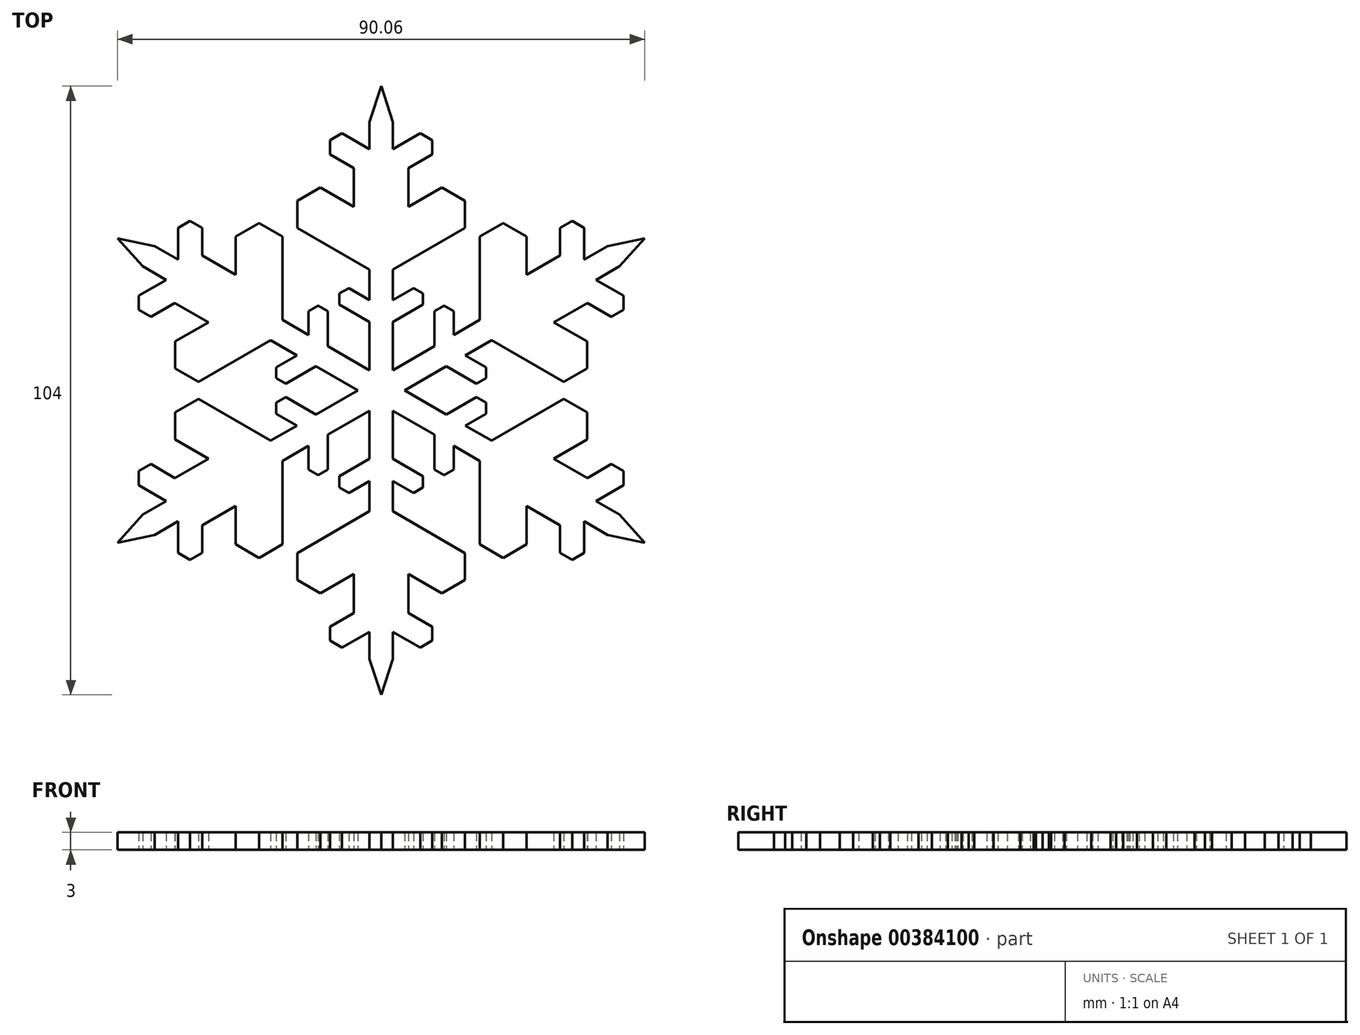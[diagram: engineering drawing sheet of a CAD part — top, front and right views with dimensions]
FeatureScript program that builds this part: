
annotation { "Feature Type Name" : "Feature", "Feature Type Description" : "" }
export const myFeature = defineFeature(function(context is Context, id is Id, definition is map)
    precondition{}
    {
        {
            var Q0;
            Q0=qCreatedBy(makeId("Top.planeOp"),FACE);
            var sketch = newSketch(context, id + "F0", { "sketchPlane" : qUnion([Q0])});
            skLineSegment(sketch, "E0", {"start": v(0, 26) * mm, "end": v(0, -26) * mm, "construction": true});
            skLineSegment(sketch, "E1", {"start": v(22.52, -13) * mm, "end": v(-22.52, 13) * mm, "construction": true});
            skLineSegment(sketch, "E2", {"start": v(-22.52, -13) * mm, "end": v(22.52, 13) * mm, "construction": true});
            skLineSegment(sketch, "E3", {"start": v(0, 26) * mm, "end": v(-1, 22.94) * mm});
            skLineSegment(sketch, "E4", {"start": v(-1, 22.94) * mm, "end": v(-1, 0.58) * mm});
            skLineSegment(sketch, "E5", {"start": v(-1, 10.33) * mm, "end": v(-7.17, 13.89) * mm});
            skLineSegment(sketch, "E6", {"start": v(-7.17, 13.89) * mm, "end": v(-7.17, 16.19) * mm});
            skLineSegment(sketch, "E7", {"start": v(-7.17, 16.19) * mm, "end": v(-5.18, 17.34) * mm});
            skLineSegment(sketch, "E8", {"start": v(-5.18, 17.34) * mm, "end": v(-2.34, 15.7) * mm});
            skLineSegment(sketch, "E9", {"start": v(-2.34, 15.7) * mm, "end": v(-2.34, 19) * mm});
            skLineSegment(sketch, "E10", {"start": v(-2.34, 19) * mm, "end": v(-4.38, 20.18) * mm});
            skLineSegment(sketch, "E11", {"start": v(-4.38, 20.18) * mm, "end": v(-4.38, 21.38) * mm});
            skLineSegment(sketch, "E12", {"start": v(-4.38, 21.38) * mm, "end": v(-3.34, 21.98) * mm});
            skLineSegment(sketch, "E13", {"start": v(-3.34, 21.98) * mm, "end": v(-1, 20.62) * mm});
            skLineSegment(sketch, "E14", {"start": v(-7.17, 13.89) * mm, "end": v(-5.18, 17.34) * mm, "construction": true});
            skLineSegment(sketch, "E15", {"start": v(-7.17, 16.19) * mm, "end": v(-6.18, 15.61) * mm, "construction": true});
            skLineSegment(sketch, "E16", {"start": v(-4.38, 20.18) * mm, "end": v(-3.34, 21.98) * mm, "construction": true});
            skLineSegment(sketch, "E17", {"start": v(-4.38, 21.38) * mm, "end": v(-3.86, 21.08) * mm, "construction": true});
            skLineSegment(sketch, "E18", {"start": v(-1, 7.73) * mm, "end": v(-2.76, 8.75) * mm});
            skLineSegment(sketch, "E19", {"start": v(-2.76, 8.75) * mm, "end": v(-3.58, 8.28) * mm});
            skLineSegment(sketch, "E20", {"start": v(-3.58, 8.28) * mm, "end": v(-3.58, 7.34) * mm});
            skLineSegment(sketch, "E21", {"start": v(-3.58, 7.34) * mm, "end": v(-1, 5.85) * mm});
            skLineSegment(sketch, "E22", {"start": v(-2.76, 8.75) * mm, "end": v(-3.58, 7.34) * mm, "construction": true});
            skLineSegment(sketch, "E23", {"start": v(-3.58, 8.28) * mm, "end": v(-3.17, 8.04) * mm, "construction": true});
            skLineSegment(sketch, "E24.MirrorCS", {"start": v(4.38, 20.18) * mm, "end": v(3.34, 21.98) * mm, "construction": true});
            skLineSegment(sketch, "E25.MirrorCS", {"start": v(3.58, 8.28) * mm, "end": v(3.58, 7.34) * mm});
            skLineSegment(sketch, "E26.MirrorCS", {"start": v(2.76, 8.75) * mm, "end": v(3.58, 7.34) * mm, "construction": true});
            skLineSegment(sketch, "E27.MirrorCS", {"start": v(3.58, 8.28) * mm, "end": v(3.17, 8.04) * mm, "construction": true});
            skLineSegment(sketch, "E28.MirrorCS", {"start": v(4.38, 21.38) * mm, "end": v(3.34, 21.98) * mm});
            skLineSegment(sketch, "E29.MirrorCS", {"start": v(2.76, 8.75) * mm, "end": v(3.58, 8.28) * mm});
            skLineSegment(sketch, "E30.MirrorCS", {"start": v(4.38, 20.18) * mm, "end": v(4.38, 21.38) * mm});
            skLineSegment(sketch, "E31.MirrorCS", {"start": v(4.38, 21.38) * mm, "end": v(3.86, 21.08) * mm, "construction": true});
            skLineSegment(sketch, "E32.MirrorCS", {"start": v(1, 7.73) * mm, "end": v(2.76, 8.75) * mm});
            skLineSegment(sketch, "E33.MirrorCS", {"start": v(7.17, 16.19) * mm, "end": v(6.18, 15.61) * mm, "construction": true});
            skLineSegment(sketch, "E34.MirrorCS", {"start": v(2.34, 19) * mm, "end": v(4.38, 20.18) * mm});
            skLineSegment(sketch, "E35.MirrorCS", {"start": v(3.58, 7.34) * mm, "end": v(1, 5.85) * mm});
            skLineSegment(sketch, "E36.MirrorCS", {"start": v(7.17, 13.89) * mm, "end": v(5.18, 17.34) * mm, "construction": true});
            skLineSegment(sketch, "E37.MirrorCS", {"start": v(0, 26) * mm, "end": v(1, 22.94) * mm});
            skLineSegment(sketch, "E38.MirrorCS", {"start": v(2.34, 15.7) * mm, "end": v(2.34, 19) * mm});
            skLineSegment(sketch, "E39.MirrorCS", {"start": v(1, 22.94) * mm, "end": v(1, 0.58) * mm});
            skLineSegment(sketch, "E40.MirrorCS", {"start": v(7.17, 13.89) * mm, "end": v(7.17, 16.19) * mm});
            skLineSegment(sketch, "E41.MirrorCS", {"start": v(5.18, 17.34) * mm, "end": v(2.34, 15.7) * mm});
            skLineSegment(sketch, "E42.MirrorCS", {"start": v(1, 10.33) * mm, "end": v(7.17, 13.89) * mm});
            skLineSegment(sketch, "E43.MirrorCS", {"start": v(7.17, 16.19) * mm, "end": v(5.18, 17.34) * mm});
            skLineSegment(sketch, "E44.MirrorCS", {"start": v(3.34, 21.98) * mm, "end": v(1, 20.62) * mm});
            skLineSegment(sketch, "E45.1.0", {"start": v(-17.6, 1.88) * mm, "end": v(-17.6, 4.18) * mm});
            skLineSegment(sketch, "E45.1.1", {"start": v(-4.56, 6.77) * mm, "end": v(-4.56, 3.79) * mm});
            skLineSegment(sketch, "E45.1.2", {"start": v(-9.44, 4.3) * mm, "end": v(-15.61, 0.73) * mm});
            skLineSegment(sketch, "E45.1.3", {"start": v(-15.61, 0.73) * mm, "end": v(-17.6, 1.88) * mm});
            skLineSegment(sketch, "E45.1.4", {"start": v(-8.44, 6.03) * mm, "end": v(-8.44, 13.15) * mm});
            skLineSegment(sketch, "E45.1.5", {"start": v(-17.6, 4.18) * mm, "end": v(-14.76, 5.82) * mm});
            skLineSegment(sketch, "E45.1.6", {"start": v(-20.36, 10.6) * mm, "end": v(-1, -0.58) * mm});
            skLineSegment(sketch, "E45.1.7", {"start": v(-22.52, 13) * mm, "end": v(-20.36, 10.6) * mm});
            skLineSegment(sketch, "E45.1.8", {"start": v(-14.76, 5.82) * mm, "end": v(-17.62, 7.47) * mm});
            skLineSegment(sketch, "E45.1.9", {"start": v(-8.44, 13.15) * mm, "end": v(-12.42, 13.15) * mm, "construction": true});
            skLineSegment(sketch, "E45.1.10", {"start": v(-15.61, 0.73) * mm, "end": v(-17.6, 4.18) * mm, "construction": true});
            skLineSegment(sketch, "E45.1.11", {"start": v(-20.7, 8.1) * mm, "end": v(-18.36, 9.45) * mm});
            skLineSegment(sketch, "E45.1.12", {"start": v(-19.36, 12.34) * mm, "end": v(0, 1.15) * mm});
            skLineSegment(sketch, "E45.1.13", {"start": v(-10.43, 14.3) * mm, "end": v(-12.42, 13.15) * mm});
            skLineSegment(sketch, "E45.1.14", {"start": v(-6.2, 4.73) * mm, "end": v(-6.2, 6.77) * mm});
            skLineSegment(sketch, "E45.1.15", {"start": v(-17.36, 13.88) * mm, "end": v(-17.36, 11.18) * mm});
            skLineSegment(sketch, "E45.1.16", {"start": v(-8.44, 13.15) * mm, "end": v(-10.43, 14.3) * mm});
            skLineSegment(sketch, "E45.1.17", {"start": v(-8.14, 0.57) * mm, "end": v(-5.56, 2.06) * mm});
            skLineSegment(sketch, "E45.1.18", {"start": v(-22.52, 13) * mm, "end": v(-19.36, 12.34) * mm});
            skLineSegment(sketch, "E45.1.19", {"start": v(-12.42, 13.15) * mm, "end": v(-12.42, 9.87) * mm});
            skLineSegment(sketch, "E45.1.20", {"start": v(-12.42, 9.87) * mm, "end": v(-15.29, 11.52) * mm});
            skLineSegment(sketch, "E45.1.21", {"start": v(-15.29, 11.52) * mm, "end": v(-15.29, 13.88) * mm});
            skLineSegment(sketch, "E45.1.22", {"start": v(-17.62, 7.47) * mm, "end": v(-19.67, 6.3) * mm});
            skLineSegment(sketch, "E45.1.23", {"start": v(-17.6, 1.88) * mm, "end": v(-16.6, 2.46) * mm, "construction": true});
            skLineSegment(sketch, "E45.1.24", {"start": v(-15.29, 13.88) * mm, "end": v(-17.36, 13.88) * mm, "construction": true});
            skLineSegment(sketch, "E45.1.25", {"start": v(-10.43, 14.3) * mm, "end": v(-10.43, 13.15) * mm, "construction": true});
            skLineSegment(sketch, "E45.1.26", {"start": v(-7.2, 3) * mm, "end": v(-8.96, 1.98) * mm});
            skLineSegment(sketch, "E45.1.27", {"start": v(-8.96, 1.04) * mm, "end": v(-8.14, 0.57) * mm});
            skLineSegment(sketch, "E45.1.28", {"start": v(-19.67, 6.3) * mm, "end": v(-20.7, 6.9) * mm});
            skLineSegment(sketch, "E45.1.29", {"start": v(-20.7, 6.9) * mm, "end": v(-20.7, 8.1) * mm});
            skLineSegment(sketch, "E45.1.30", {"start": v(-8.96, 1.04) * mm, "end": v(-8.55, 1.28) * mm, "construction": true});
            skLineSegment(sketch, "E45.1.31", {"start": v(-6.2, 6.77) * mm, "end": v(-5.38, 7.24) * mm});
            skLineSegment(sketch, "E45.1.32", {"start": v(-5.38, 7.24) * mm, "end": v(-5.38, 6.77) * mm, "construction": true});
            skLineSegment(sketch, "E45.1.33", {"start": v(-6.2, 6.77) * mm, "end": v(-4.56, 6.77) * mm, "construction": true});
            skLineSegment(sketch, "E45.1.34", {"start": v(-8.96, 1.98) * mm, "end": v(-8.96, 1.04) * mm});
            skLineSegment(sketch, "E45.1.35", {"start": v(-19.67, 6.3) * mm, "end": v(-20.7, 8.1) * mm, "construction": true});
            skLineSegment(sketch, "E45.1.36", {"start": v(-16.32, 14.48) * mm, "end": v(-17.36, 13.88) * mm});
            skLineSegment(sketch, "E45.1.37", {"start": v(-15.29, 13.88) * mm, "end": v(-16.32, 14.48) * mm});
            skLineSegment(sketch, "E45.1.38", {"start": v(-20.7, 6.9) * mm, "end": v(-20.18, 7.2) * mm, "construction": true});
            skLineSegment(sketch, "E45.1.39", {"start": v(-5.38, 7.24) * mm, "end": v(-4.56, 6.77) * mm});
            skLineSegment(sketch, "E45.1.40", {"start": v(-8.96, 1.98) * mm, "end": v(-8.14, 0.57) * mm, "construction": true});
            skLineSegment(sketch, "E45.1.41", {"start": v(-16.32, 14.48) * mm, "end": v(-16.32, 13.88) * mm, "construction": true});
            skLineSegment(sketch, "E45.2.0", {"start": v(-10.43, -14.3) * mm, "end": v(-12.42, -13.15) * mm});
            skLineSegment(sketch, "E45.2.1", {"start": v(-8.14, -0.57) * mm, "end": v(-5.56, -2.06) * mm});
            skLineSegment(sketch, "E45.2.2", {"start": v(-8.44, -6.03) * mm, "end": v(-8.44, -13.15) * mm});
            skLineSegment(sketch, "E45.2.3", {"start": v(-8.44, -13.15) * mm, "end": v(-10.43, -14.3) * mm});
            skLineSegment(sketch, "E45.2.4", {"start": v(-9.44, -4.3) * mm, "end": v(-15.61, -0.73) * mm});
            skLineSegment(sketch, "E45.2.5", {"start": v(-12.42, -13.15) * mm, "end": v(-12.42, -9.87) * mm});
            skLineSegment(sketch, "E45.2.6", {"start": v(-19.36, -12.34) * mm, "end": v(0, -1.15) * mm});
            skLineSegment(sketch, "E45.2.7", {"start": v(-22.52, -13) * mm, "end": v(-19.36, -12.34) * mm});
            skLineSegment(sketch, "E45.2.8", {"start": v(-12.42, -9.87) * mm, "end": v(-15.29, -11.52) * mm});
            skLineSegment(sketch, "E45.2.9", {"start": v(-15.61, -0.73) * mm, "end": v(-17.6, -4.18) * mm, "construction": true});
            skLineSegment(sketch, "E45.2.10", {"start": v(-8.44, -13.15) * mm, "end": v(-12.42, -13.15) * mm, "construction": true});
            skLineSegment(sketch, "E45.2.11", {"start": v(-17.36, -13.88) * mm, "end": v(-17.36, -11.18) * mm});
            skLineSegment(sketch, "E45.2.12", {"start": v(-20.36, -10.6) * mm, "end": v(-1, 0.58) * mm});
            skLineSegment(sketch, "E45.2.13", {"start": v(-17.6, -1.88) * mm, "end": v(-17.6, -4.18) * mm});
            skLineSegment(sketch, "E45.2.14", {"start": v(-7.2, -3) * mm, "end": v(-8.96, -1.98) * mm});
            skLineSegment(sketch, "E45.2.15", {"start": v(-20.7, -8.1) * mm, "end": v(-18.36, -9.45) * mm});
            skLineSegment(sketch, "E45.2.16", {"start": v(-15.61, -0.73) * mm, "end": v(-17.6, -1.88) * mm});
            skLineSegment(sketch, "E45.2.17", {"start": v(-4.56, -6.77) * mm, "end": v(-4.56, -3.79) * mm});
            skLineSegment(sketch, "E45.2.18", {"start": v(-22.52, -13) * mm, "end": v(-20.36, -10.6) * mm});
            skLineSegment(sketch, "E45.2.19", {"start": v(-17.6, -4.18) * mm, "end": v(-14.76, -5.82) * mm});
            skLineSegment(sketch, "E45.2.20", {"start": v(-14.76, -5.82) * mm, "end": v(-17.62, -7.47) * mm});
            skLineSegment(sketch, "E45.2.21", {"start": v(-17.62, -7.47) * mm, "end": v(-19.67, -6.3) * mm});
            skLineSegment(sketch, "E45.2.22", {"start": v(-15.29, -11.52) * mm, "end": v(-15.29, -13.88) * mm});
            skLineSegment(sketch, "E45.2.23", {"start": v(-10.43, -14.3) * mm, "end": v(-10.43, -13.15) * mm, "construction": true});
            skLineSegment(sketch, "E45.2.24", {"start": v(-19.67, -6.3) * mm, "end": v(-20.7, -8.1) * mm, "construction": true});
            skLineSegment(sketch, "E45.2.25", {"start": v(-17.6, -1.88) * mm, "end": v(-16.6, -2.46) * mm, "construction": true});
            skLineSegment(sketch, "E45.2.26", {"start": v(-6.2, -4.73) * mm, "end": v(-6.2, -6.77) * mm});
            skLineSegment(sketch, "E45.2.27", {"start": v(-5.38, -7.24) * mm, "end": v(-4.56, -6.77) * mm});
            skLineSegment(sketch, "E45.2.28", {"start": v(-15.29, -13.88) * mm, "end": v(-16.32, -14.48) * mm});
            skLineSegment(sketch, "E45.2.29", {"start": v(-16.32, -14.48) * mm, "end": v(-17.36, -13.88) * mm});
            skLineSegment(sketch, "E45.2.30", {"start": v(-5.38, -7.24) * mm, "end": v(-5.38, -6.77) * mm, "construction": true});
            skLineSegment(sketch, "E45.2.31", {"start": v(-8.96, -1.98) * mm, "end": v(-8.96, -1.04) * mm});
            skLineSegment(sketch, "E45.2.32", {"start": v(-8.96, -1.04) * mm, "end": v(-8.55, -1.28) * mm, "construction": true});
            skLineSegment(sketch, "E45.2.33", {"start": v(-8.96, -1.98) * mm, "end": v(-8.14, -0.57) * mm, "construction": true});
            skLineSegment(sketch, "E45.2.34", {"start": v(-6.2, -6.77) * mm, "end": v(-5.38, -7.24) * mm});
            skLineSegment(sketch, "E45.2.35", {"start": v(-15.29, -13.88) * mm, "end": v(-17.36, -13.88) * mm, "construction": true});
            skLineSegment(sketch, "E45.2.36", {"start": v(-20.7, -6.9) * mm, "end": v(-20.7, -8.1) * mm});
            skLineSegment(sketch, "E45.2.37", {"start": v(-19.67, -6.3) * mm, "end": v(-20.7, -6.9) * mm});
            skLineSegment(sketch, "E45.2.38", {"start": v(-16.32, -14.48) * mm, "end": v(-16.32, -13.88) * mm, "construction": true});
            skLineSegment(sketch, "E45.2.39", {"start": v(-8.96, -1.04) * mm, "end": v(-8.14, -0.57) * mm});
            skLineSegment(sketch, "E45.2.40", {"start": v(-6.2, -6.77) * mm, "end": v(-4.56, -6.77) * mm, "construction": true});
            skLineSegment(sketch, "E45.2.41", {"start": v(-20.7, -6.9) * mm, "end": v(-20.18, -7.2) * mm, "construction": true});
            skLineSegment(sketch, "E45.3.0", {"start": v(7.17, -16.19) * mm, "end": v(5.18, -17.34) * mm});
            skLineSegment(sketch, "E45.3.1", {"start": v(-3.58, -7.34) * mm, "end": v(-1, -5.85) * mm});
            skLineSegment(sketch, "E45.3.2", {"start": v(1, -10.33) * mm, "end": v(7.17, -13.89) * mm});
            skLineSegment(sketch, "E45.3.3", {"start": v(7.17, -13.89) * mm, "end": v(7.17, -16.19) * mm});
            skLineSegment(sketch, "E45.3.4", {"start": v(-1, -10.33) * mm, "end": v(-7.17, -13.89) * mm});
            skLineSegment(sketch, "E45.3.5", {"start": v(5.18, -17.34) * mm, "end": v(2.34, -15.7) * mm});
            skLineSegment(sketch, "E45.3.6", {"start": v(1, -22.94) * mm, "end": v(1, -0.58) * mm});
            skLineSegment(sketch, "E45.3.7", {"start": v(0, -26) * mm, "end": v(1, -22.94) * mm});
            skLineSegment(sketch, "E45.3.8", {"start": v(2.34, -15.7) * mm, "end": v(2.34, -19) * mm});
            skLineSegment(sketch, "E45.3.9", {"start": v(-7.17, -13.89) * mm, "end": v(-5.18, -17.34) * mm, "construction": true});
            skLineSegment(sketch, "E45.3.10", {"start": v(7.17, -13.89) * mm, "end": v(5.18, -17.34) * mm, "construction": true});
            skLineSegment(sketch, "E45.3.11", {"start": v(3.34, -21.98) * mm, "end": v(1, -20.62) * mm});
            skLineSegment(sketch, "E45.3.12", {"start": v(-1, -22.94) * mm, "end": v(-1, -0.58) * mm});
            skLineSegment(sketch, "E45.3.13", {"start": v(-7.17, -16.19) * mm, "end": v(-5.18, -17.34) * mm});
            skLineSegment(sketch, "E45.3.14", {"start": v(-1, -7.73) * mm, "end": v(-2.76, -8.75) * mm});
            skLineSegment(sketch, "E45.3.15", {"start": v(-3.34, -21.98) * mm, "end": v(-1, -20.62) * mm});
            skLineSegment(sketch, "E45.3.16", {"start": v(-7.17, -13.89) * mm, "end": v(-7.17, -16.19) * mm});
            skLineSegment(sketch, "E45.3.17", {"start": v(3.58, -7.34) * mm, "end": v(1, -5.85) * mm});
            skLineSegment(sketch, "E45.3.18", {"start": v(0, -26) * mm, "end": v(-1, -22.94) * mm});
            skLineSegment(sketch, "E45.3.19", {"start": v(-5.18, -17.34) * mm, "end": v(-2.34, -15.7) * mm});
            skLineSegment(sketch, "E45.3.20", {"start": v(-2.34, -15.7) * mm, "end": v(-2.34, -19) * mm});
            skLineSegment(sketch, "E45.3.21", {"start": v(-2.34, -19) * mm, "end": v(-4.38, -20.18) * mm});
            skLineSegment(sketch, "E45.3.22", {"start": v(2.34, -19) * mm, "end": v(4.38, -20.18) * mm});
            skLineSegment(sketch, "E45.3.23", {"start": v(7.17, -16.19) * mm, "end": v(6.18, -15.61) * mm, "construction": true});
            skLineSegment(sketch, "E45.3.24", {"start": v(-4.38, -20.18) * mm, "end": v(-3.34, -21.98) * mm, "construction": true});
            skLineSegment(sketch, "E45.3.25", {"start": v(-7.17, -16.19) * mm, "end": v(-6.18, -15.61) * mm, "construction": true});
            skLineSegment(sketch, "E45.3.26", {"start": v(1, -7.73) * mm, "end": v(2.76, -8.75) * mm});
            skLineSegment(sketch, "E45.3.27", {"start": v(3.58, -8.28) * mm, "end": v(3.58, -7.34) * mm});
            skLineSegment(sketch, "E45.3.28", {"start": v(4.38, -20.18) * mm, "end": v(4.38, -21.38) * mm});
            skLineSegment(sketch, "E45.3.29", {"start": v(4.38, -21.38) * mm, "end": v(3.34, -21.98) * mm});
            skLineSegment(sketch, "E45.3.30", {"start": v(3.58, -8.28) * mm, "end": v(3.17, -8.04) * mm, "construction": true});
            skLineSegment(sketch, "E45.3.31", {"start": v(-2.76, -8.75) * mm, "end": v(-3.58, -8.28) * mm});
            skLineSegment(sketch, "E45.3.32", {"start": v(-3.58, -8.28) * mm, "end": v(-3.17, -8.04) * mm, "construction": true});
            skLineSegment(sketch, "E45.3.33", {"start": v(-2.76, -8.75) * mm, "end": v(-3.58, -7.34) * mm, "construction": true});
            skLineSegment(sketch, "E45.3.34", {"start": v(2.76, -8.75) * mm, "end": v(3.58, -8.28) * mm});
            skLineSegment(sketch, "E45.3.35", {"start": v(4.38, -20.18) * mm, "end": v(3.34, -21.98) * mm, "construction": true});
            skLineSegment(sketch, "E45.3.36", {"start": v(-4.38, -21.38) * mm, "end": v(-3.34, -21.98) * mm});
            skLineSegment(sketch, "E45.3.37", {"start": v(-4.38, -20.18) * mm, "end": v(-4.38, -21.38) * mm});
            skLineSegment(sketch, "E45.3.38", {"start": v(4.38, -21.38) * mm, "end": v(3.86, -21.08) * mm, "construction": true});
            skLineSegment(sketch, "E45.3.39", {"start": v(-3.58, -8.28) * mm, "end": v(-3.58, -7.34) * mm});
            skLineSegment(sketch, "E45.3.40", {"start": v(2.76, -8.75) * mm, "end": v(3.58, -7.34) * mm, "construction": true});
            skLineSegment(sketch, "E45.3.41", {"start": v(-4.38, -21.38) * mm, "end": v(-3.86, -21.08) * mm, "construction": true});
            skLineSegment(sketch, "E45.4.0", {"start": v(17.6, -1.88) * mm, "end": v(17.6, -4.18) * mm});
            skLineSegment(sketch, "E45.4.1", {"start": v(4.56, -6.77) * mm, "end": v(4.56, -3.79) * mm});
            skLineSegment(sketch, "E45.4.2", {"start": v(9.44, -4.3) * mm, "end": v(15.61, -0.73) * mm});
            skLineSegment(sketch, "E45.4.3", {"start": v(15.61, -0.73) * mm, "end": v(17.6, -1.88) * mm});
            skLineSegment(sketch, "E45.4.4", {"start": v(8.44, -6.03) * mm, "end": v(8.44, -13.15) * mm});
            skLineSegment(sketch, "E45.4.5", {"start": v(17.6, -4.18) * mm, "end": v(14.76, -5.82) * mm});
            skLineSegment(sketch, "E45.4.6", {"start": v(20.36, -10.6) * mm, "end": v(1, 0.58) * mm});
            skLineSegment(sketch, "E45.4.7", {"start": v(22.52, -13) * mm, "end": v(20.36, -10.6) * mm});
            skLineSegment(sketch, "E45.4.8", {"start": v(14.76, -5.82) * mm, "end": v(17.62, -7.47) * mm});
            skLineSegment(sketch, "E45.4.9", {"start": v(8.44, -13.15) * mm, "end": v(12.42, -13.15) * mm, "construction": true});
            skLineSegment(sketch, "E45.4.10", {"start": v(15.61, -0.73) * mm, "end": v(17.6, -4.18) * mm, "construction": true});
            skLineSegment(sketch, "E45.4.11", {"start": v(20.7, -8.1) * mm, "end": v(18.36, -9.45) * mm});
            skLineSegment(sketch, "E45.4.12", {"start": v(19.36, -12.34) * mm, "end": v(0, -1.15) * mm});
            skLineSegment(sketch, "E45.4.13", {"start": v(10.43, -14.3) * mm, "end": v(12.42, -13.15) * mm});
            skLineSegment(sketch, "E45.4.14", {"start": v(6.2, -4.73) * mm, "end": v(6.2, -6.77) * mm});
            skLineSegment(sketch, "E45.4.15", {"start": v(17.36, -13.88) * mm, "end": v(17.36, -11.18) * mm});
            skLineSegment(sketch, "E45.4.16", {"start": v(8.44, -13.15) * mm, "end": v(10.43, -14.3) * mm});
            skLineSegment(sketch, "E45.4.17", {"start": v(8.14, -0.57) * mm, "end": v(5.56, -2.06) * mm});
            skLineSegment(sketch, "E45.4.18", {"start": v(22.52, -13) * mm, "end": v(19.36, -12.34) * mm});
            skLineSegment(sketch, "E45.4.19", {"start": v(12.42, -13.15) * mm, "end": v(12.42, -9.87) * mm});
            skLineSegment(sketch, "E45.4.20", {"start": v(12.42, -9.87) * mm, "end": v(15.29, -11.52) * mm});
            skLineSegment(sketch, "E45.4.21", {"start": v(15.29, -11.52) * mm, "end": v(15.29, -13.88) * mm});
            skLineSegment(sketch, "E45.4.22", {"start": v(17.62, -7.47) * mm, "end": v(19.67, -6.3) * mm});
            skLineSegment(sketch, "E45.4.23", {"start": v(17.6, -1.88) * mm, "end": v(16.6, -2.46) * mm, "construction": true});
            skLineSegment(sketch, "E45.4.24", {"start": v(15.29, -13.88) * mm, "end": v(17.36, -13.88) * mm, "construction": true});
            skLineSegment(sketch, "E45.4.25", {"start": v(10.43, -14.3) * mm, "end": v(10.43, -13.15) * mm, "construction": true});
            skLineSegment(sketch, "E45.4.26", {"start": v(7.2, -3) * mm, "end": v(8.96, -1.98) * mm});
            skLineSegment(sketch, "E45.4.27", {"start": v(8.96, -1.04) * mm, "end": v(8.14, -0.57) * mm});
            skLineSegment(sketch, "E45.4.28", {"start": v(19.67, -6.3) * mm, "end": v(20.7, -6.9) * mm});
            skLineSegment(sketch, "E45.4.29", {"start": v(20.7, -6.9) * mm, "end": v(20.7, -8.1) * mm});
            skLineSegment(sketch, "E45.4.30", {"start": v(8.96, -1.04) * mm, "end": v(8.55, -1.28) * mm, "construction": true});
            skLineSegment(sketch, "E45.4.31", {"start": v(6.2, -6.77) * mm, "end": v(5.38, -7.24) * mm});
            skLineSegment(sketch, "E45.4.32", {"start": v(5.38, -7.24) * mm, "end": v(5.38, -6.77) * mm, "construction": true});
            skLineSegment(sketch, "E45.4.33", {"start": v(6.2, -6.77) * mm, "end": v(4.56, -6.77) * mm, "construction": true});
            skLineSegment(sketch, "E45.4.34", {"start": v(8.96, -1.98) * mm, "end": v(8.96, -1.04) * mm});
            skLineSegment(sketch, "E45.4.35", {"start": v(19.67, -6.3) * mm, "end": v(20.7, -8.1) * mm, "construction": true});
            skLineSegment(sketch, "E45.4.36", {"start": v(16.32, -14.48) * mm, "end": v(17.36, -13.88) * mm});
            skLineSegment(sketch, "E45.4.37", {"start": v(15.29, -13.88) * mm, "end": v(16.32, -14.48) * mm});
            skLineSegment(sketch, "E45.4.38", {"start": v(20.7, -6.9) * mm, "end": v(20.18, -7.2) * mm, "construction": true});
            skLineSegment(sketch, "E45.4.39", {"start": v(5.38, -7.24) * mm, "end": v(4.56, -6.77) * mm});
            skLineSegment(sketch, "E45.4.40", {"start": v(8.96, -1.98) * mm, "end": v(8.14, -0.57) * mm, "construction": true});
            skLineSegment(sketch, "E45.4.41", {"start": v(16.32, -14.48) * mm, "end": v(16.32, -13.88) * mm, "construction": true});
            skLineSegment(sketch, "E45.5.0", {"start": v(10.43, 14.3) * mm, "end": v(12.42, 13.15) * mm});
            skLineSegment(sketch, "E45.5.1", {"start": v(8.14, 0.57) * mm, "end": v(5.56, 2.06) * mm});
            skLineSegment(sketch, "E45.5.2", {"start": v(8.44, 6.03) * mm, "end": v(8.44, 13.15) * mm});
            skLineSegment(sketch, "E45.5.3", {"start": v(8.44, 13.15) * mm, "end": v(10.43, 14.3) * mm});
            skLineSegment(sketch, "E45.5.4", {"start": v(9.44, 4.3) * mm, "end": v(15.61, 0.73) * mm});
            skLineSegment(sketch, "E45.5.5", {"start": v(12.42, 13.15) * mm, "end": v(12.42, 9.87) * mm});
            skLineSegment(sketch, "E45.5.6", {"start": v(19.36, 12.34) * mm, "end": v(0, 1.15) * mm});
            skLineSegment(sketch, "E45.5.7", {"start": v(22.52, 13) * mm, "end": v(19.36, 12.34) * mm});
            skLineSegment(sketch, "E45.5.8", {"start": v(12.42, 9.87) * mm, "end": v(15.29, 11.52) * mm});
            skLineSegment(sketch, "E45.5.9", {"start": v(15.61, 0.73) * mm, "end": v(17.6, 4.18) * mm, "construction": true});
            skLineSegment(sketch, "E45.5.10", {"start": v(8.44, 13.15) * mm, "end": v(12.42, 13.15) * mm, "construction": true});
            skLineSegment(sketch, "E45.5.11", {"start": v(17.36, 13.88) * mm, "end": v(17.36, 11.18) * mm});
            skLineSegment(sketch, "E45.5.12", {"start": v(20.36, 10.6) * mm, "end": v(1, -0.58) * mm});
            skLineSegment(sketch, "E45.5.13", {"start": v(17.6, 1.88) * mm, "end": v(17.6, 4.18) * mm});
            skLineSegment(sketch, "E45.5.14", {"start": v(7.2, 3) * mm, "end": v(8.96, 1.98) * mm});
            skLineSegment(sketch, "E45.5.15", {"start": v(20.7, 8.1) * mm, "end": v(18.36, 9.45) * mm});
            skLineSegment(sketch, "E45.5.16", {"start": v(15.61, 0.73) * mm, "end": v(17.6, 1.88) * mm});
            skLineSegment(sketch, "E45.5.17", {"start": v(4.56, 6.77) * mm, "end": v(4.56, 3.79) * mm});
            skLineSegment(sketch, "E45.5.18", {"start": v(22.52, 13) * mm, "end": v(20.36, 10.6) * mm});
            skLineSegment(sketch, "E45.5.19", {"start": v(17.6, 4.18) * mm, "end": v(14.76, 5.82) * mm});
            skLineSegment(sketch, "E45.5.20", {"start": v(14.76, 5.82) * mm, "end": v(17.62, 7.47) * mm});
            skLineSegment(sketch, "E45.5.21", {"start": v(17.62, 7.47) * mm, "end": v(19.67, 6.3) * mm});
            skLineSegment(sketch, "E45.5.22", {"start": v(15.29, 11.52) * mm, "end": v(15.29, 13.88) * mm});
            skLineSegment(sketch, "E45.5.23", {"start": v(10.43, 14.3) * mm, "end": v(10.43, 13.15) * mm, "construction": true});
            skLineSegment(sketch, "E45.5.24", {"start": v(19.67, 6.3) * mm, "end": v(20.7, 8.1) * mm, "construction": true});
            skLineSegment(sketch, "E45.5.25", {"start": v(17.6, 1.88) * mm, "end": v(16.6, 2.46) * mm, "construction": true});
            skLineSegment(sketch, "E45.5.26", {"start": v(6.2, 4.73) * mm, "end": v(6.2, 6.77) * mm});
            skLineSegment(sketch, "E45.5.27", {"start": v(5.38, 7.24) * mm, "end": v(4.56, 6.77) * mm});
            skLineSegment(sketch, "E45.5.28", {"start": v(15.29, 13.88) * mm, "end": v(16.32, 14.48) * mm});
            skLineSegment(sketch, "E45.5.29", {"start": v(16.32, 14.48) * mm, "end": v(17.36, 13.88) * mm});
            skLineSegment(sketch, "E45.5.30", {"start": v(5.38, 7.24) * mm, "end": v(5.38, 6.77) * mm, "construction": true});
            skLineSegment(sketch, "E45.5.31", {"start": v(8.96, 1.98) * mm, "end": v(8.96, 1.04) * mm});
            skLineSegment(sketch, "E45.5.32", {"start": v(8.96, 1.04) * mm, "end": v(8.55, 1.28) * mm, "construction": true});
            skLineSegment(sketch, "E45.5.33", {"start": v(8.96, 1.98) * mm, "end": v(8.14, 0.57) * mm, "construction": true});
            skLineSegment(sketch, "E45.5.34", {"start": v(6.2, 6.77) * mm, "end": v(5.38, 7.24) * mm});
            skLineSegment(sketch, "E45.5.35", {"start": v(15.29, 13.88) * mm, "end": v(17.36, 13.88) * mm, "construction": true});
            skLineSegment(sketch, "E45.5.36", {"start": v(20.7, 6.9) * mm, "end": v(20.7, 8.1) * mm});
            skLineSegment(sketch, "E45.5.37", {"start": v(19.67, 6.3) * mm, "end": v(20.7, 6.9) * mm});
            skLineSegment(sketch, "E45.5.38", {"start": v(16.32, 14.48) * mm, "end": v(16.32, 13.88) * mm, "construction": true});
            skLineSegment(sketch, "E45.5.39", {"start": v(8.96, 1.04) * mm, "end": v(8.14, 0.57) * mm});
            skLineSegment(sketch, "E45.5.40", {"start": v(6.2, 6.77) * mm, "end": v(4.56, 6.77) * mm, "construction": true});
            skLineSegment(sketch, "E45.5.41", {"start": v(20.7, 6.9) * mm, "end": v(20.18, 7.2) * mm, "construction": true});
            skPoint(sketch, "E45.center", {"position": v(0, 0) * mm});
            skSolve(sketch);
        }
        {
            var Q0;
            Q0 = qSketchRegion(id + "F0", true);
            extrude(context, id + "F1", {"entities" : qUnion([Q0]), "depth" : 1.5 * mm});
        }
        {
            var Q0;
            Q0=makeQuery(id+"F1.opExtrude","SWEPT_BODY",BODY,{"disambiguationData":[OSD([sQuery(id+"F0.wireOp",EDGE,"E3"),sQuery(id+"F0.wireOp",EDGE,"E4"),sQuery(id+"F0.wireOp",EDGE,"E5"),sQuery(id+"F0.wireOp",EDGE,"E6"),sQuery(id+"F0.wireOp",EDGE,"E7"),sQuery(id+"F0.wireOp",EDGE,"E8"),sQuery(id+"F0.wireOp",EDGE,"E9"),sQuery(id+"F0.wireOp",EDGE,"E10"),sQuery(id+"F0.wireOp",EDGE,"E11"),sQuery(id+"F0.wireOp",EDGE,"E12"),sQuery(id+"F0.wireOp",EDGE,"E13"),sQuery(id+"F0.wireOp",EDGE,"E18"),sQuery(id+"F0.wireOp",EDGE,"E19"),sQuery(id+"F0.wireOp",EDGE,"E20"),sQuery(id+"F0.wireOp",EDGE,"E21"),sQuery(id+"F0.wireOp",EDGE,"E25.MirrorCS"),sQuery(id+"F0.wireOp",EDGE,"E28.MirrorCS"),sQuery(id+"F0.wireOp",EDGE,"E29.MirrorCS"),sQuery(id+"F0.wireOp",EDGE,"E30.MirrorCS"),sQuery(id+"F0.wireOp",EDGE,"E32.MirrorCS"),sQuery(id+"F0.wireOp",EDGE,"E34.MirrorCS"),sQuery(id+"F0.wireOp",EDGE,"E35.MirrorCS"),sQuery(id+"F0.wireOp",EDGE,"E37.MirrorCS"),sQuery(id+"F0.wireOp",EDGE,"E38.MirrorCS"),sQuery(id+"F0.wireOp",EDGE,"E39.MirrorCS"),sQuery(id+"F0.wireOp",EDGE,"E40.MirrorCS"),sQuery(id+"F0.wireOp",EDGE,"E41.MirrorCS"),sQuery(id+"F0.wireOp",EDGE,"E42.MirrorCS"),sQuery(id+"F0.wireOp",EDGE,"E43.MirrorCS"),sQuery(id+"F0.wireOp",EDGE,"E44.MirrorCS"),sQuery(id+"F0.wireOp",EDGE,"E45.1.0"),sQuery(id+"F0.wireOp",EDGE,"E45.1.1"),sQuery(id+"F0.wireOp",EDGE,"E45.1.2"),sQuery(id+"F0.wireOp",EDGE,"E45.1.3"),sQuery(id+"F0.wireOp",EDGE,"E45.1.4"),sQuery(id+"F0.wireOp",EDGE,"E45.1.5"),sQuery(id+"F0.wireOp",EDGE,"E45.1.6"),sQuery(id+"F0.wireOp",EDGE,"E45.1.7"),sQuery(id+"F0.wireOp",EDGE,"E45.1.8"),sQuery(id+"F0.wireOp",EDGE,"E45.1.11"),sQuery(id+"F0.wireOp",EDGE,"E45.1.12"),sQuery(id+"F0.wireOp",EDGE,"E45.1.13"),sQuery(id+"F0.wireOp",EDGE,"E45.1.14"),sQuery(id+"F0.wireOp",EDGE,"E45.1.15"),sQuery(id+"F0.wireOp",EDGE,"E45.1.16"),sQuery(id+"F0.wireOp",EDGE,"E45.1.17"),sQuery(id+"F0.wireOp",EDGE,"E45.1.18"),sQuery(id+"F0.wireOp",EDGE,"E45.1.19"),sQuery(id+"F0.wireOp",EDGE,"E45.1.20"),sQuery(id+"F0.wireOp",EDGE,"E45.1.21"),sQuery(id+"F0.wireOp",EDGE,"E45.1.22"),sQuery(id+"F0.wireOp",EDGE,"E45.1.26"),sQuery(id+"F0.wireOp",EDGE,"E45.1.27"),sQuery(id+"F0.wireOp",EDGE,"E45.1.28"),sQuery(id+"F0.wireOp",EDGE,"E45.1.29"),sQuery(id+"F0.wireOp",EDGE,"E45.1.31"),sQuery(id+"F0.wireOp",EDGE,"E45.1.34"),sQuery(id+"F0.wireOp",EDGE,"E45.1.36"),sQuery(id+"F0.wireOp",EDGE,"E45.1.37"),sQuery(id+"F0.wireOp",EDGE,"E45.1.39"),sQuery(id+"F0.wireOp",EDGE,"E45.2.0"),sQuery(id+"F0.wireOp",EDGE,"E45.2.1"),sQuery(id+"F0.wireOp",EDGE,"E45.2.2"),sQuery(id+"F0.wireOp",EDGE,"E45.2.3"),sQuery(id+"F0.wireOp",EDGE,"E45.2.4"),sQuery(id+"F0.wireOp",EDGE,"E45.2.5"),sQuery(id+"F0.wireOp",EDGE,"E45.2.6"),sQuery(id+"F0.wireOp",EDGE,"E45.2.7"),sQuery(id+"F0.wireOp",EDGE,"E45.2.8"),sQuery(id+"F0.wireOp",EDGE,"E45.2.11"),sQuery(id+"F0.wireOp",EDGE,"E45.2.12"),sQuery(id+"F0.wireOp",EDGE,"E45.2.13"),sQuery(id+"F0.wireOp",EDGE,"E45.2.14"),sQuery(id+"F0.wireOp",EDGE,"E45.2.15"),sQuery(id+"F0.wireOp",EDGE,"E45.2.16"),sQuery(id+"F0.wireOp",EDGE,"E45.2.17"),sQuery(id+"F0.wireOp",EDGE,"E45.2.18"),sQuery(id+"F0.wireOp",EDGE,"E45.2.19"),sQuery(id+"F0.wireOp",EDGE,"E45.2.20"),sQuery(id+"F0.wireOp",EDGE,"E45.2.21"),sQuery(id+"F0.wireOp",EDGE,"E45.2.22"),sQuery(id+"F0.wireOp",EDGE,"E45.2.26"),sQuery(id+"F0.wireOp",EDGE,"E45.2.27"),sQuery(id+"F0.wireOp",EDGE,"E45.2.28"),sQuery(id+"F0.wireOp",EDGE,"E45.2.29"),sQuery(id+"F0.wireOp",EDGE,"E45.2.31"),sQuery(id+"F0.wireOp",EDGE,"E45.2.34"),sQuery(id+"F0.wireOp",EDGE,"E45.2.36"),sQuery(id+"F0.wireOp",EDGE,"E45.2.37"),sQuery(id+"F0.wireOp",EDGE,"E45.2.39"),sQuery(id+"F0.wireOp",EDGE,"E45.3.0"),sQuery(id+"F0.wireOp",EDGE,"E45.3.1"),sQuery(id+"F0.wireOp",EDGE,"E45.3.2"),sQuery(id+"F0.wireOp",EDGE,"E45.3.3"),sQuery(id+"F0.wireOp",EDGE,"E45.3.4"),sQuery(id+"F0.wireOp",EDGE,"E45.3.5"),sQuery(id+"F0.wireOp",EDGE,"E45.3.6"),sQuery(id+"F0.wireOp",EDGE,"E45.3.7"),sQuery(id+"F0.wireOp",EDGE,"E45.3.8"),sQuery(id+"F0.wireOp",EDGE,"E45.3.11"),sQuery(id+"F0.wireOp",EDGE,"E45.3.12"),sQuery(id+"F0.wireOp",EDGE,"E45.3.13"),sQuery(id+"F0.wireOp",EDGE,"E45.3.14"),sQuery(id+"F0.wireOp",EDGE,"E45.3.15"),sQuery(id+"F0.wireOp",EDGE,"E45.3.16"),sQuery(id+"F0.wireOp",EDGE,"E45.3.17"),sQuery(id+"F0.wireOp",EDGE,"E45.3.18"),sQuery(id+"F0.wireOp",EDGE,"E45.3.19"),sQuery(id+"F0.wireOp",EDGE,"E45.3.20"),sQuery(id+"F0.wireOp",EDGE,"E45.3.21"),sQuery(id+"F0.wireOp",EDGE,"E45.3.22"),sQuery(id+"F0.wireOp",EDGE,"E45.3.26"),sQuery(id+"F0.wireOp",EDGE,"E45.3.27"),sQuery(id+"F0.wireOp",EDGE,"E45.3.28"),sQuery(id+"F0.wireOp",EDGE,"E45.3.29"),sQuery(id+"F0.wireOp",EDGE,"E45.3.31"),sQuery(id+"F0.wireOp",EDGE,"E45.3.34"),sQuery(id+"F0.wireOp",EDGE,"E45.3.36"),sQuery(id+"F0.wireOp",EDGE,"E45.3.37"),sQuery(id+"F0.wireOp",EDGE,"E45.3.39"),sQuery(id+"F0.wireOp",EDGE,"E45.4.0"),sQuery(id+"F0.wireOp",EDGE,"E45.4.1"),sQuery(id+"F0.wireOp",EDGE,"E45.4.2"),sQuery(id+"F0.wireOp",EDGE,"E45.4.3"),sQuery(id+"F0.wireOp",EDGE,"E45.4.4"),sQuery(id+"F0.wireOp",EDGE,"E45.4.5"),sQuery(id+"F0.wireOp",EDGE,"E45.4.6"),sQuery(id+"F0.wireOp",EDGE,"E45.4.7"),sQuery(id+"F0.wireOp",EDGE,"E45.4.8"),sQuery(id+"F0.wireOp",EDGE,"E45.4.11"),sQuery(id+"F0.wireOp",EDGE,"E45.4.12"),sQuery(id+"F0.wireOp",EDGE,"E45.4.13"),sQuery(id+"F0.wireOp",EDGE,"E45.4.14"),sQuery(id+"F0.wireOp",EDGE,"E45.4.15"),sQuery(id+"F0.wireOp",EDGE,"E45.4.16"),sQuery(id+"F0.wireOp",EDGE,"E45.4.17"),sQuery(id+"F0.wireOp",EDGE,"E45.4.18"),sQuery(id+"F0.wireOp",EDGE,"E45.4.19"),sQuery(id+"F0.wireOp",EDGE,"E45.4.20"),sQuery(id+"F0.wireOp",EDGE,"E45.4.21"),sQuery(id+"F0.wireOp",EDGE,"E45.4.22"),sQuery(id+"F0.wireOp",EDGE,"E45.4.26"),sQuery(id+"F0.wireOp",EDGE,"E45.4.27"),sQuery(id+"F0.wireOp",EDGE,"E45.4.28"),sQuery(id+"F0.wireOp",EDGE,"E45.4.29"),sQuery(id+"F0.wireOp",EDGE,"E45.4.31"),sQuery(id+"F0.wireOp",EDGE,"E45.4.34"),sQuery(id+"F0.wireOp",EDGE,"E45.4.36"),sQuery(id+"F0.wireOp",EDGE,"E45.4.37"),sQuery(id+"F0.wireOp",EDGE,"E45.4.39"),sQuery(id+"F0.wireOp",EDGE,"E45.5.0"),sQuery(id+"F0.wireOp",EDGE,"E45.5.1"),sQuery(id+"F0.wireOp",EDGE,"E45.5.2"),sQuery(id+"F0.wireOp",EDGE,"E45.5.3"),sQuery(id+"F0.wireOp",EDGE,"E45.5.4"),sQuery(id+"F0.wireOp",EDGE,"E45.5.5"),sQuery(id+"F0.wireOp",EDGE,"E45.5.6"),sQuery(id+"F0.wireOp",EDGE,"E45.5.7"),sQuery(id+"F0.wireOp",EDGE,"E45.5.8"),sQuery(id+"F0.wireOp",EDGE,"E45.5.11"),sQuery(id+"F0.wireOp",EDGE,"E45.5.12"),sQuery(id+"F0.wireOp",EDGE,"E45.5.13"),sQuery(id+"F0.wireOp",EDGE,"E45.5.14"),sQuery(id+"F0.wireOp",EDGE,"E45.5.15"),sQuery(id+"F0.wireOp",EDGE,"E45.5.16"),sQuery(id+"F0.wireOp",EDGE,"E45.5.17"),sQuery(id+"F0.wireOp",EDGE,"E45.5.18"),sQuery(id+"F0.wireOp",EDGE,"E45.5.19"),sQuery(id+"F0.wireOp",EDGE,"E45.5.20"),sQuery(id+"F0.wireOp",EDGE,"E45.5.21"),sQuery(id+"F0.wireOp",EDGE,"E45.5.22"),sQuery(id+"F0.wireOp",EDGE,"E45.5.26"),sQuery(id+"F0.wireOp",EDGE,"E45.5.27"),sQuery(id+"F0.wireOp",EDGE,"E45.5.28"),sQuery(id+"F0.wireOp",EDGE,"E45.5.29"),sQuery(id+"F0.wireOp",EDGE,"E45.5.31"),sQuery(id+"F0.wireOp",EDGE,"E45.5.34"),sQuery(id+"F0.wireOp",EDGE,"E45.5.36"),sQuery(id+"F0.wireOp",EDGE,"E45.5.37"),sQuery(id+"F0.wireOp",EDGE,"E45.5.39")])]});
            var Q1;
            Q1=qCreatedBy(makeId("Origin.pointOp"),VERTEX);
            transform(context, id + "F2", {"entities" : qUnion([Q0]), "transformType" : TransformType.SCALE_UNIFORMLY, "scale" : 2, "scalePoint" : qUnion([Q1]), "makeCopy" : false});
        }
    });
